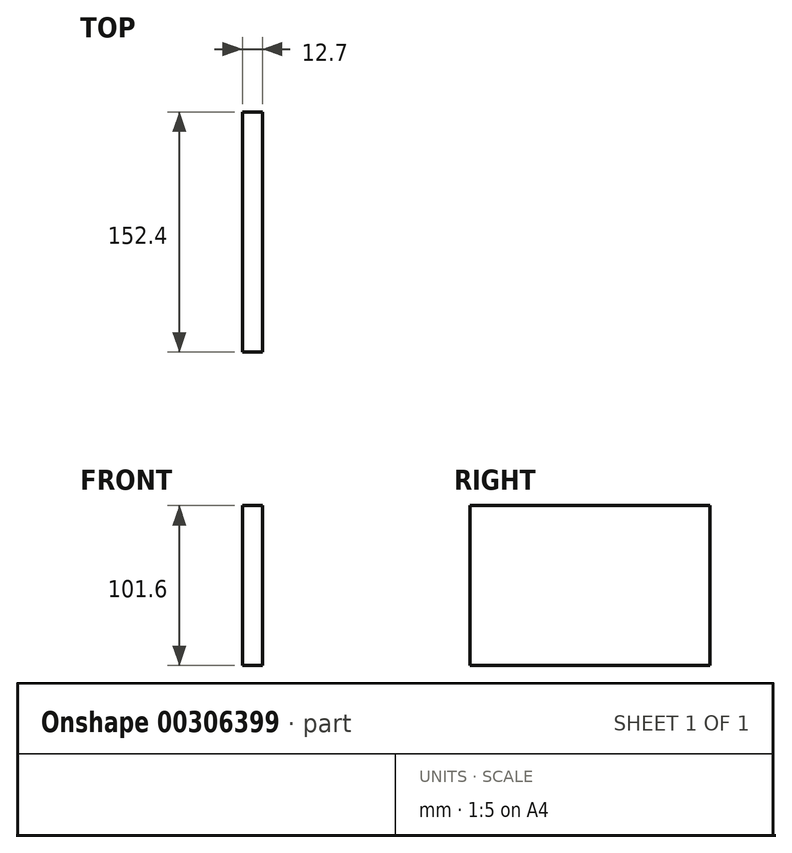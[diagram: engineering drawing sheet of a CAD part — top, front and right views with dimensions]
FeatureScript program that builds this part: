
annotation { "Feature Type Name" : "Feature", "Feature Type Description" : "" }
export const myFeature = defineFeature(function(context is Context, id is Id, definition is map)
    precondition{}
    {
        {
            var Q0;
            Q0=qCreatedBy(makeId("Right.planeOp"),FACE);
            var sketch = newSketch(context, id + "F0", { "sketchPlane" : qUnion([Q0])});
            skLineSegment(sketch, "E0.bottom", {"start": v(76.2, -50.8) * mm, "end": v(-76.2, -50.8) * mm});
            skLineSegment(sketch, "E0.top", {"start": v(76.2, 50.8) * mm, "end": v(-76.2, 50.8) * mm});
            skLineSegment(sketch, "E0.left", {"start": v(76.2, -50.8) * mm, "end": v(76.2, 50.8) * mm});
            skLineSegment(sketch, "E0.right", {"start": v(-76.2, -50.8) * mm, "end": v(-76.2, 50.8) * mm});
            skPoint(sketch, "E0.middle", {"position": v(0, 0) * mm});
            skSolve(sketch);
        }
        {
            var Q0;
            Q0 = qSketchRegion(id + "F0", true);
            extrude(context, id + "F1", {"entities" : qUnion([Q0]), "depth" : 12.7 * mm});
        }
    });
